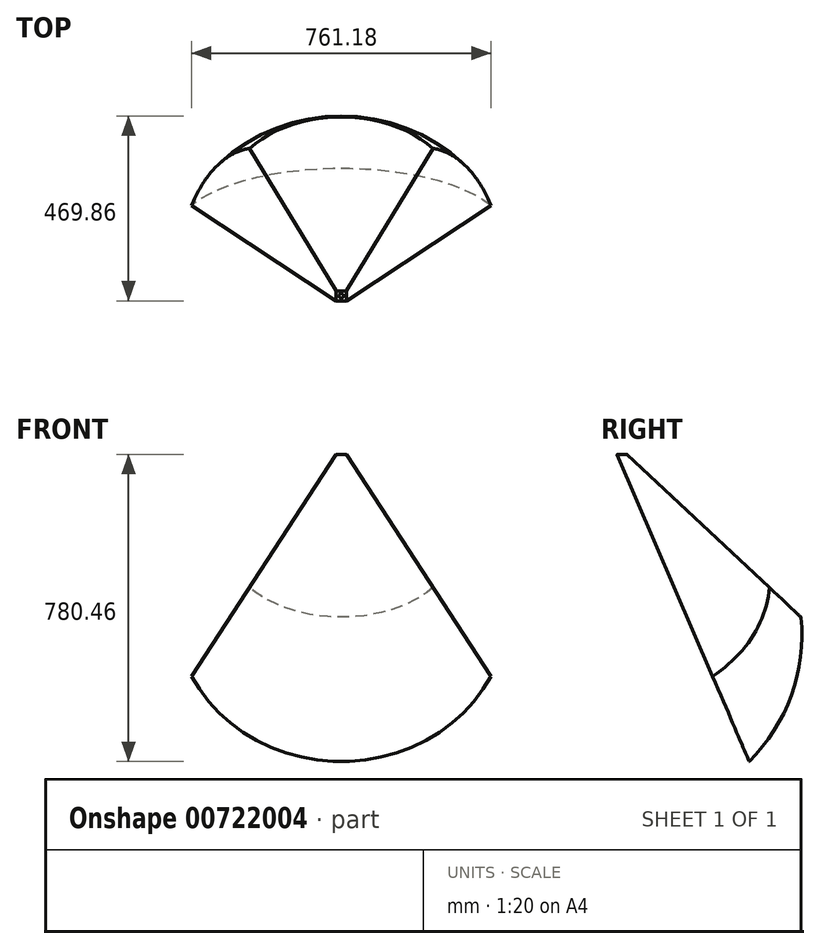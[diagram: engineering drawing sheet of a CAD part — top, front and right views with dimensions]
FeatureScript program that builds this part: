
annotation { "Feature Type Name" : "Feature", "Feature Type Description" : "" }
export const myFeature = defineFeature(function(context is Context, id is Id, definition is map)
    precondition{}
    {
        {
            var Q0;
            Q0=qCreatedBy(makeId("Top.planeOp"),FACE);
            var sketch = newSketch(context, id + "F0", { "sketchPlane" : qUnion([Q0])});
            skLineSegment(sketch, "E0.bottom", {"start": v(-609.6, 990.6) * mm, "end": v(609.6, 990.6) * mm});
            skLineSegment(sketch, "E0.top", {"start": v(-609.6, 381) * mm, "end": v(609.6, 381) * mm});
            skLineSegment(sketch, "E0.left", {"start": v(-609.6, 990.6) * mm, "end": v(-609.6, 381) * mm});
            skLineSegment(sketch, "E0.right", {"start": v(609.6, 990.6) * mm, "end": v(609.6, 381) * mm});
            skPoint(sketch, "E1", {"position": v(0, 990.6) * mm});
            skSolve(sketch);
        }
        {
            var Q0;
            Q0=qCreatedBy(makeId("Top.planeOp"),FACE);
            cPlane(context, id + "F1", {"entities" : qUnion([Q0]), "cplaneType" : CPlaneType.OFFSET, "offset" : 914.4 * mm, "width" : 152.4 * mm, "height" : 152.4 * mm});
        }
        {
            var Q0;
            Q0=qCreatedBy(id+"F1.planeOp",FACE);
            var sketch = newSketch(context, id + "F2", { "sketchPlane" : qUnion([Q0])});
            skLineSegment(sketch, "E2.bottom", {"start": v(-12.7, 12.7) * mm, "end": v(12.7, 12.7) * mm});
            skLineSegment(sketch, "E2.top", {"start": v(-12.7, -12.7) * mm, "end": v(12.7, -12.7) * mm});
            skLineSegment(sketch, "E2.left", {"start": v(-12.7, 12.7) * mm, "end": v(-12.7, -12.7) * mm});
            skLineSegment(sketch, "E2.right", {"start": v(12.7, 12.7) * mm, "end": v(12.7, -12.7) * mm});
            skPoint(sketch, "E3", {"position": v(0, 12.7) * mm});
            skPoint(sketch, "E4", {"position": v(12.7, 0) * mm});
            skSolve(sketch);
        }
        {
            var Q0;
            Q0=makeQuery(id+"F2.imprint","IMPRINT",FACE,{"disambiguationData":[TD([[makeQuery(id+"F2.imprint","IMPRINT",EDGE,{"derivedFrom":sQuery(id+"F2.wireOp",EDGE,"E2.bottom")}),-1.0]])]});
            var Q1;
            Q1=makeQuery(id+"F0.imprint","IMPRINT",FACE,{"disambiguationData":[TD([[makeQuery(id+"F0.imprint","IMPRINT",EDGE,{"derivedFrom":sQuery(id+"F0.wireOp",EDGE,"E0.bottom")}),-1.0]])]});
            loft(context, id + "F3", {"sheetProfilesArray" : [{ "sheetProfileEntities" : qUnion([Q0]) }, { "sheetProfileEntities" : qUnion([Q1]) }]});
        }
        {
            var Q0;
            Q0=qCreatedBy(makeId("Right.planeOp"),FACE);
            var sketch = newSketch(context, id + "F4", { "sketchPlane" : qUnion([Q0])});
            skLineSegment(sketch, "E5", {"start": v(0, 914.44) * mm, "end": v(0, 0) * mm});
            skPoint(sketch, "E6", {"position": v(0, 457.22) * mm});
            skArc(sketch, "E7", {"start": v(0, 0) * mm, "mid": v(457.22, 457.22) * mm, "end": v(0, 914.44) * mm});
            skSolve(sketch);
        }
        {
            var Q0;
            Q0=makeQuery(id+"F4.imprint","IMPRINT",FACE,{"disambiguationData":[TD([[makeQuery(id+"F4.imprint","IMPRINT",EDGE,{"derivedFrom":sQuery(id+"F4.wireOp",EDGE,"E5")}),1.0]])]});
            var Q1;
            Q1=sQuery(id+"F4.wireOp",EDGE,"E5");
            revolve(context, id + "F5", {"operationType" : NewBodyOperationType.INTERSECT, "surfaceOperationType" : NewSurfaceOperationType.NEW, "entities" : qUnion([Q0]), "axis" : qUnion([Q1]), "revolveType" : RevolveType.FULL});
        }
    });
